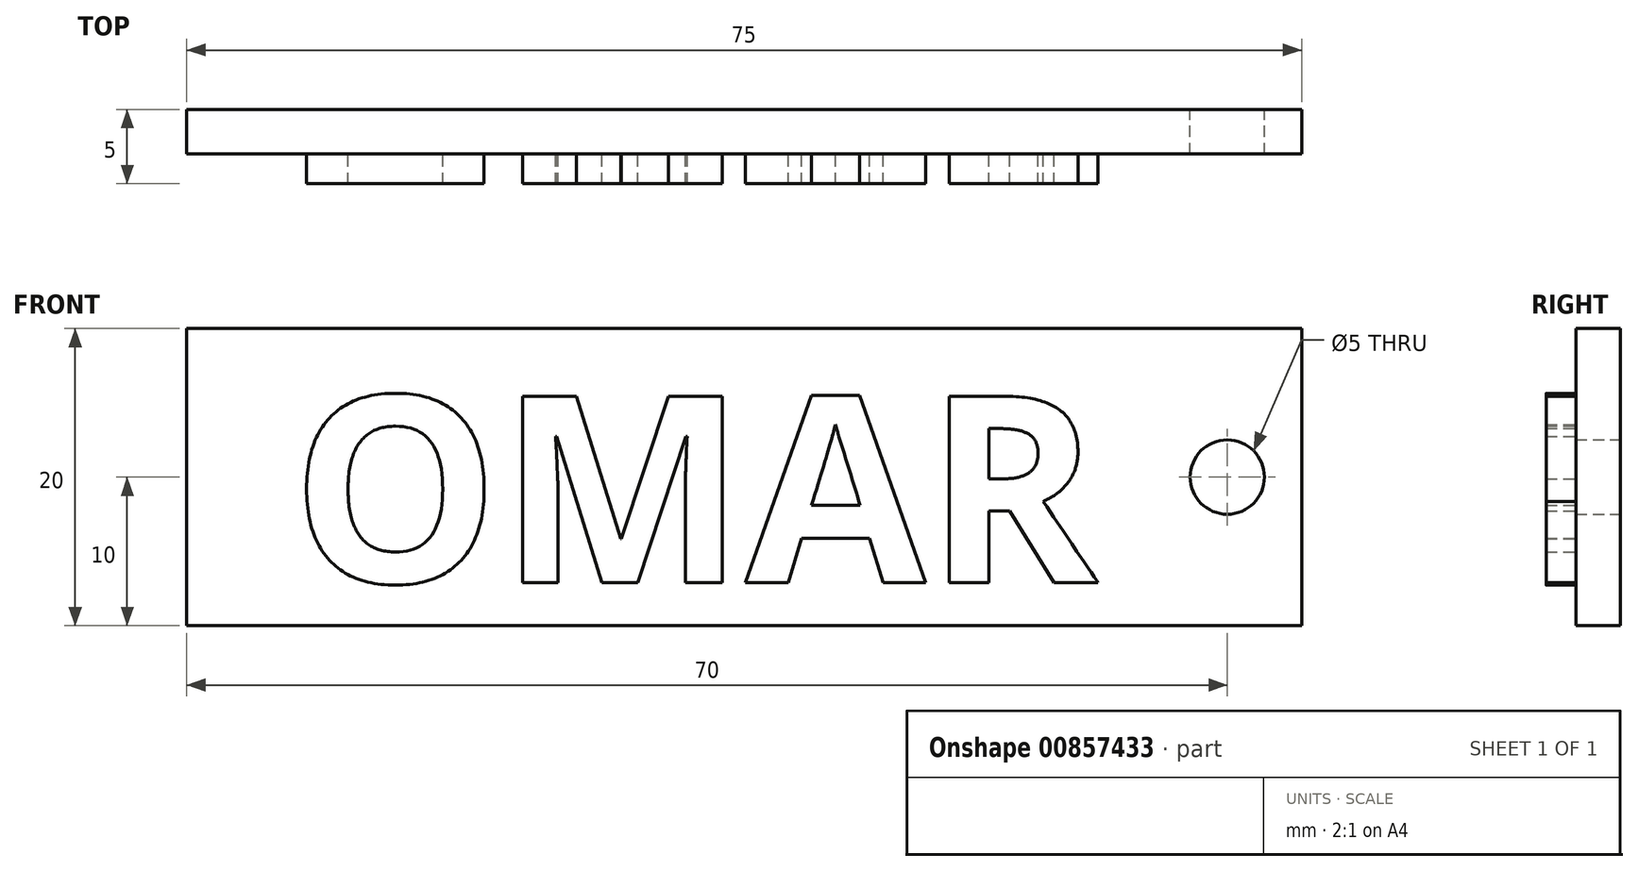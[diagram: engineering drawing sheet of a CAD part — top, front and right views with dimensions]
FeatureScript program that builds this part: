
annotation { "Feature Type Name" : "Feature", "Feature Type Description" : "" }
export const myFeature = defineFeature(function(context is Context, id is Id, definition is map)
    precondition{}
    {
        {
            var Q0;
            Q0=qCreatedBy(makeId("Front.planeOp"),FACE);
            var sketch = newSketch(context, id + "F0", { "sketchPlane" : qUnion([Q0])});
            skLineSegment(sketch, "E0.bottom", {"start": v(0, 0) * mm, "end": v(75, 0) * mm});
            skLineSegment(sketch, "E0.top", {"start": v(0, -20) * mm, "end": v(75, -20) * mm});
            skLineSegment(sketch, "E0.left", {"start": v(0, 0) * mm, "end": v(0, -20) * mm});
            skLineSegment(sketch, "E0.right", {"start": v(75, 0) * mm, "end": v(75, -20) * mm});
            skCircle(sketch, "E1", {"center": v(70, -10) * mm, "radius": 2.5 * mm});
            skPoint(sketch, "E1.centerSnap0", {"position": v(75, -10) * mm});
            skSolve(sketch);
        }
        {
            var Q0;
            Q0=makeQuery(id+"F0.imprint","IMPRINT",FACE,{"disambiguationData":[TD([[makeQuery(id+"F0.imprint","IMPRINT",EDGE,{"derivedFrom":sQuery(id+"F0.wireOp",EDGE,"E0.bottom")}),-1.0]])]});
            extrude(context, id + "F1", {"entities" : qUnion([Q0]), "depth" : 3 * mm, "offsetDistance" : 25 * mm});
        }
        {
            var Q0;
            Q0=makeQuery(id+"F1.opExtrude","CAP_FACE",FACE,{"disambiguationData":[OSD([sQuery(id+"F0.wireOp",EDGE,"E0.bottom"),sQuery(id+"F0.wireOp",EDGE,"E0.top"),sQuery(id+"F0.wireOp",EDGE,"E0.left"),sQuery(id+"F0.wireOp",EDGE,"E0.right"),sQuery(id+"F0.wireOp",EDGE,"E1")])],"isStart":false});
            var sketch = newSketch(context, id + "F2", { "sketchPlane" : qUnion([Q0])});
            skText(sketch, "E2", { "text": "OMAR", "fontName": "OpenSans-Bold.ttf"});
            const initialGuessF2  = {"E2": [0.00704, -0.0171, 1, 0, 0.01265]};
            skSetInitialGuess(sketch, initialGuessF2);
            skSolve(sketch);
        }
        {
            var Q0;
            Q0 = qSketchRegion(id + "F2", true);
            extrude(context, id + "F3", {"entities" : qUnion([Q0]), "operationType" : NewBodyOperationType.ADD, "depth" : 2 * mm, "offsetDistance" : 25 * mm});
        }
    });
